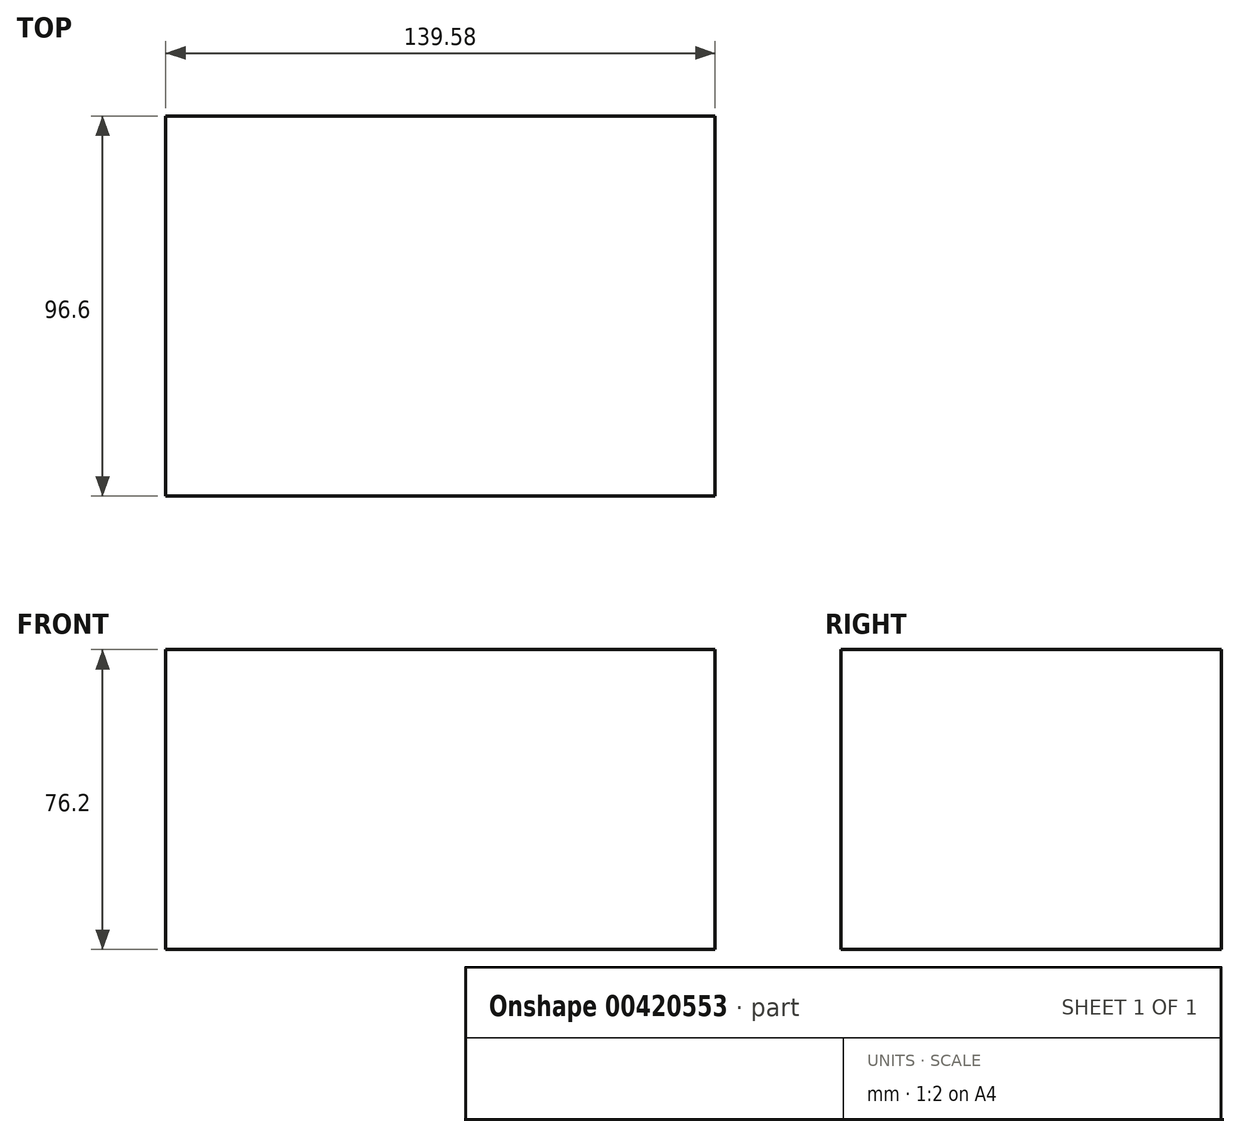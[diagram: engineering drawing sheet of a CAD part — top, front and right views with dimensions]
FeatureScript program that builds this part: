
annotation { "Feature Type Name" : "Feature", "Feature Type Description" : "" }
export const myFeature = defineFeature(function(context is Context, id is Id, definition is map)
    precondition{}
    {
        {
            var Q0;
            Q0=qCreatedBy(makeId("Top.planeOp"),FACE);
            var sketch = newSketch(context, id + "F0", { "sketchPlane" : qUnion([Q0])});
            skLineSegment(sketch, "E0.bottom", {"start": v(-69.79, -48.3) * mm, "end": v(69.79, -48.3) * mm});
            skLineSegment(sketch, "E0.top", {"start": v(-69.79, 48.3) * mm, "end": v(69.79, 48.3) * mm});
            skLineSegment(sketch, "E0.left", {"start": v(-69.79, -48.3) * mm, "end": v(-69.79, 48.3) * mm});
            skLineSegment(sketch, "E0.right", {"start": v(69.79, -48.3) * mm, "end": v(69.79, 48.3) * mm});
            skPoint(sketch, "E0.middle", {"position": v(0, 0) * mm});
            skLineSegment(sketch, "E1.bottom", {"start": v(-69.79, 48.3) * mm, "end": v(-28.17, 48.3) * mm});
            skLineSegment(sketch, "E1.top", {"start": v(-69.79, 74.87) * mm, "end": v(-28.17, 74.87) * mm});
            skLineSegment(sketch, "E1.left", {"start": v(-69.79, 48.3) * mm, "end": v(-69.79, 74.87) * mm});
            skLineSegment(sketch, "E1.right", {"start": v(-28.17, 48.3) * mm, "end": v(-28.17, 74.87) * mm});
            skSolve(sketch);
        }
        {
            var Q0;
            Q0=makeQuery(id+"F0.imprint","IMPRINT",FACE,{"disambiguationData":[TD([[makeQuery(id+"F0.imprint","IMPRINT",EDGE,{"derivedFrom":sQuery(id+"F0.wireOp",EDGE,"E0.bottom")}),1.0]])]});
            extrude(context, id + "F1", {"entities" : qUnion([Q0]), "depth" : 76.2 * mm});
        }
    });
